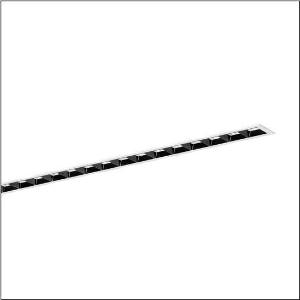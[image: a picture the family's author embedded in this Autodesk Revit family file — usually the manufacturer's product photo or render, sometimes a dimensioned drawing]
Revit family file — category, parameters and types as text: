
# Revit family: silica_r__21_51mx11tat4w_b1e5
name_source: partatom
category: Lighting Fixtures
units: mm (PartAtom-declared; Revit-internal decimal feet)

## family parameters
Cut with Voids When Loaded = No
Host = Face
Light Source = No
Part Type = Normal
Room Calculation Point = No
Round Connector Dimension = Use Diameter
Shared = No

## types (1)
- --- (1 x LED, 3720 lm, 32.2 W, 6500K)
    Apparent Load = 32 VA
    CIE Flux Codes = 85 99 100 100 100
    Color Rendering = 80
    Color Temperature = 6500K
    Default Elevation = 1800 mm
    Description = Silica® 21, office luminaire, primary light control with darklight reflector, of PMMA, black, CAT 2 (L<= 3000cd/m²), light emission: direct distribution, primary light characteristic: symmetric, installation type: recessed, LED, rated luminous flux: 3.720lm, luminous efficacy: 110lm/W, light colour: 8tw, colour temperature: 2700..6500K, with terminal, 3+2-pole, max. 2.5mm², mains connection: 220..240V, AC, 50/60Hz, rated input power: 33.8W, luminaire housing, of aluminium, traffic white (RAL 9016), length: 1.228mm, width: 79mm, height: 53mm, protection rating (complete): IP20, insulation class (complete): insulation class I (protective earthing), certification: CE, permissible operating ambient temperature: 0..+35°C, standard: EN 50419, packaging unit: 1 piece
    Height = 0 mm  [stored 0 ft]
    Lamp = 1 x LED
    Lamp Light Flux = 3720 lm
    Lamp Power = 32.2 W
    Lamp count = 1
    Length = 1227 mm
    Luminous efficacy = 116 lm/W
    Manufacturer = Siteco
    ModVariant = No
    Model = 51MX11TAT4W
    Mounting Place = Ceiling
    Mounting Type = Recessed
    Number of Poles = 1
    OnlyDefault = Yes
    Power Factor = 1
    Product Name = Silica® 21
    Product group = office luminaire | ceiling recessed
    ProductGroupID = 401
    Protection Class = Protection class I
    Protection Degree = IP 20
    RLX_Detail_Level = 1
    RLX_Emergency_Light_Flux = 0 lm
    RLX_Emergency_Type = 0
    RLX_Emergency_Type_DB = No
    RlxData = <blob elided: 35649 chars, md5=8ac87ee6>
    Socket = socket
    Standby Power = 0 W
    System Light Flux = 3720 lm
    System Power = 32 W
    Type Comments = individual setting
    Type Image = l_1313610.jpg
    URL = http://relux.com
    VarID = @adj_089475
    Voltage = 0 V
    Weight = 0.00 kg
    Width = 79 mm

note: [stored X ft] marks values corroborated as IEEE doubles in the binary element streams (Revit-internal decimal feet)

## geometry (parser evidence)
native form markers: Blend x4, Sweep x9
no freeform markers — native parametric forms only
